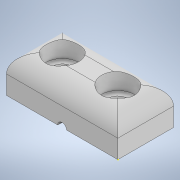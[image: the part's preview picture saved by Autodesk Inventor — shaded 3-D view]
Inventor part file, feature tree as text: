
AUTODESK INVENTOR PART (.ipt)
format: ipt  version: 2020 (Build 240168000, 168)  size: 145,408 bytes
history: native  units: in
note: dims shown in document units (in); Inventor stores cm internally (conversion verified against a paired STEP export)
features: sketch x4, hole x2, extrude x1, fillet x1
ambient origin geometry x8: Origin, YZ Plane, XZ Plane, XY Plane, X Axis, Y Axis, Z Axis, Center Point
bodies: Solid1 (feature_tree)
feature tree (8):
  extrude  "Extrusion1"  Depth=0.375in
  hole  "Hole1"  [1 undecoded]
  hole  "Hole2"  [1 undecoded]
  sketch  "Sketch4"  dims[d12=0.188in d13=0.188in d14=0.188in d15=0.129in d16=0.75in d17=0.219in d18=0.112in d19=0.5635in d20=0.25in d21=0.8108in d22=0.125in]
  fillet  "Fillet1"  Radius=0.188in
  sketch  "Sketch1"  dims[d0=0.75in d1=0.375in]
  sketch  "Sketch2"  dims[d2=0.25in d3=0.0in]
  sketch  "Sketch3"  dims[d4=0.0591in d5=0.75in d6=0.375in d7=0.25in d8=0.5635in d9=0.25in d10=0.8108in d11=0.188in]
note: 2 required parameter values undecoded (feature->parameter linkage not recoverable at this tier; creation-order binding heuristic only, values carry confidence <= 0.55)
